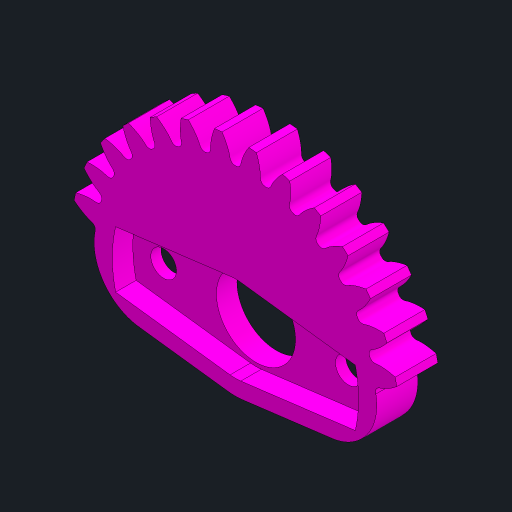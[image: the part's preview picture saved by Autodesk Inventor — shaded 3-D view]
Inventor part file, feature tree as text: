
AUTODESK INVENTOR PART (.ipt)
format: ipt  version: 2023.2 (Build 272271030, 271C)  size: 382,464 bytes
history: native  units: mm
features: sketch x5, extrude x5, pattern_circular x1, hole x1, projected_geometry x1
ambient origin geometry x8: Origin, YZ Plane, XZ Plane, XY Plane, X Axis, Y Axis, Z Axis, Center Point
bodies: Solid1 (feature_tree)
feature tree (13):
  sketch  "Sketch1"  dims[d0=4.0mm d1=0.0mm d2=0.0mm d3=0.0mm]
  extrude  "Extrusion1"  TaperAngle=0.0deg  [1 undecoded]
  extrude  "Extrusion2"  Depth=8.0mm
  pattern_circular  "Circular Pattern1"  [2 undecoded]
  extrude  "Extrusion3"  Depth=5.0mm
  extrude  "Extrusion4"  Depth=5.0mm
  hole  "Hole1"  [1 undecoded]
  extrude  "Extrusion5"  TaperAngle=0.0deg  [1 undecoded]
  sketch  "Sketch2"  dims[d4=300.0mm d5=360.0deg d7=8.0mm]
  sketch  "Sketch3"  dims[d8=32.0mm]
  sketch  "Sketch4"  dims[d9=4.0mm]
  sketch  "Sketch6"  dims[d10=4.0mm d11=4.0mm d12=0.2mm d13=24.0mm d14=2.0mm d15=0.0mm d16=0.0mm d17=0.0mm d18=18.0mm d19=9.0mm d20=2.5mm d21=6.0mm d22=6.0mm d23=1.0mm d24=90.0deg d25=8.0mm d26=20.594885mm d27=1.5mm d28=5.0mm d29=0.0mm d30=0.0mm d31=7.7mm]
  projected_geometry  "Projected Loop2"
note: 5 required parameter values undecoded (feature->parameter linkage not recoverable at this tier; creation-order binding heuristic only, values carry confidence <= 0.55)
